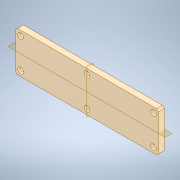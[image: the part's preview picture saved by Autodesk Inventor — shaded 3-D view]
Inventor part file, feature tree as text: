
AUTODESK INVENTOR PART (.ipt)
format: ipt  version: 2022 (Build 260153000, 153)  size: 129,536 bytes
history: native  units: mm
features: other x4, plane x2, sketch x2, reference x2, extrude x1, chamfer x1, hole x1
ambient origin geometry x8: Origin, YZ Plane, XZ Plane, XY Plane, X Axis, Y Axis, Z Axis, Center Point
bodies: Solid1 (feature_tree)
feature tree (13):
  extrude  "Extrusion1"  Depth=153.0mm
  chamfer  "Chamfer1"  Distance=6.35mm
  plane  "Work Plane1"
  plane  "Work Plane2"
  hole  "Hole1"  [1 undecoded]
  sketch  "Sketch1"  dims[d0=43.0mm d1=153.0mm d2=6.35mm d3=0.0mm]
  sketch  "Sketch2"  dims[d4=2.0mm d5=2.0mm d6=45.0deg d7=3.4mm d8=6.0mm d9=6.3mm d10=2.0mm d11=90.0deg d12=8.0mm d13=20.594885mm]
  reference  "Reference1"
  reference  "Reference2"
  parser-record x1  (decoder bookkeeping rows leaked as tree rows — omitted from the tree; the rows remain in map.json)
  other  "Main Body.iam"
  other  "Base Plate:2"
  other  "Base Plate:1"
note: 1 required parameter value undecoded (feature->parameter linkage not recoverable at this tier; creation-order binding heuristic only, values carry confidence <= 0.55)
note: 1 file-system path scrubbed to <path> (originals preserved in map.json)
